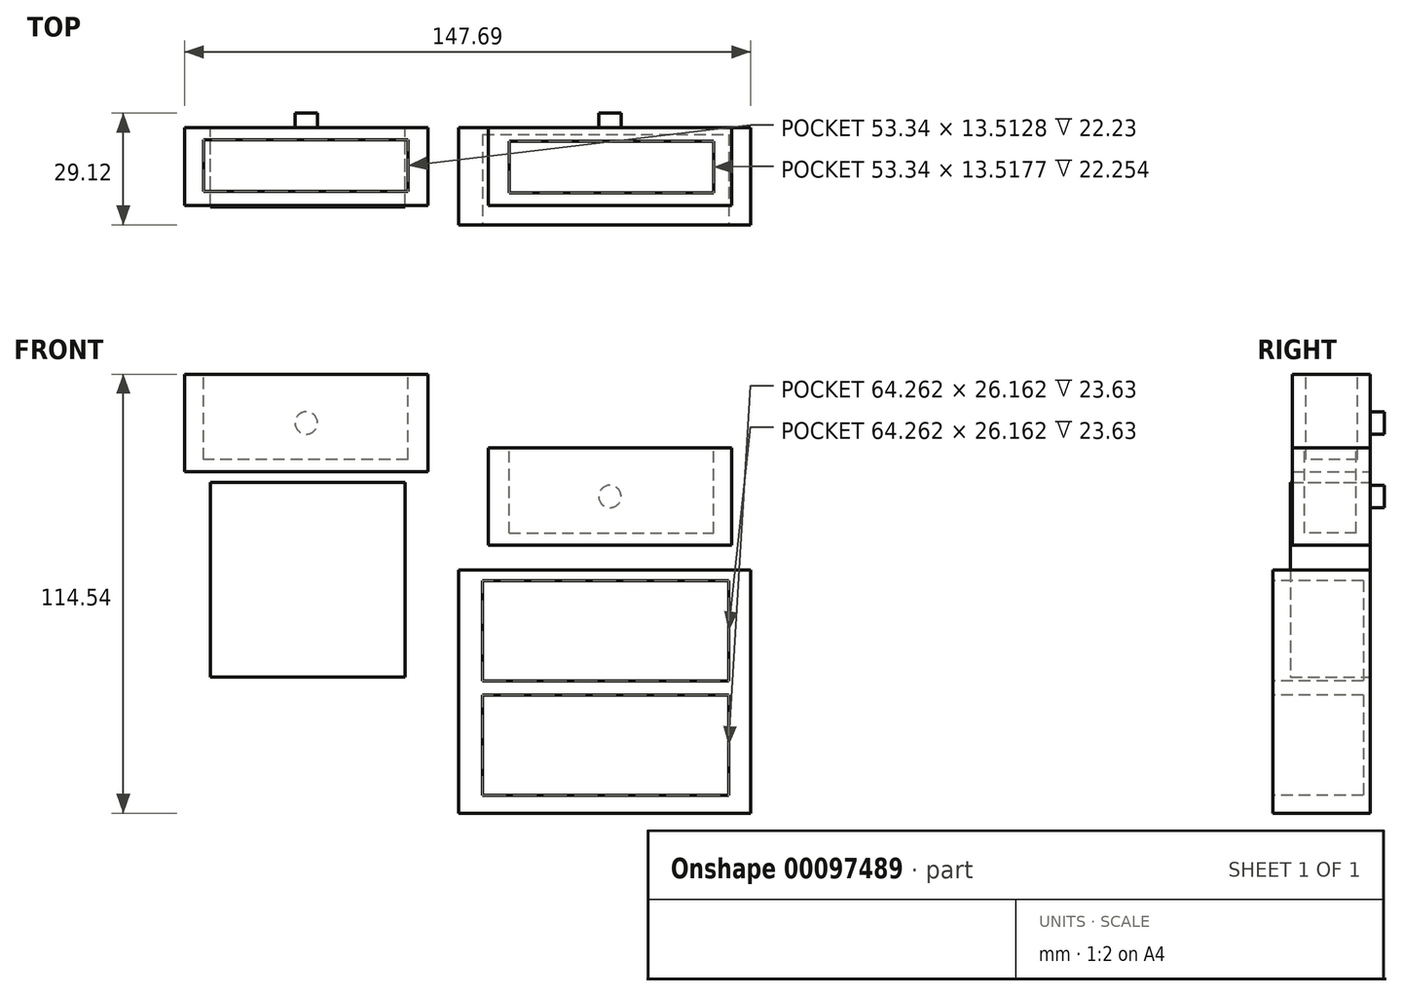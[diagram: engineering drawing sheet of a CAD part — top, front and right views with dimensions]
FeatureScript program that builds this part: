
annotation { "Feature Type Name" : "Feature", "Feature Type Description" : "" }
export const myFeature = defineFeature(function(context is Context, id is Id, definition is map)
    precondition{}
    {
        {
            var Q0;
            Q0=qCreatedBy(makeId("Front.planeOp"),FACE);
            var sketch = newSketch(context, id + "F0", { "sketchPlane" : qUnion([Q0])});
            skLineSegment(sketch, "E0.bottom", {"start": v(-64.78, 16.94) * mm, "end": v(-13.98, 16.94) * mm});
            skLineSegment(sketch, "E0.top", {"start": v(-64.78, -33.86) * mm, "end": v(-13.98, -33.86) * mm});
            skLineSegment(sketch, "E0.left", {"start": v(-64.78, 16.94) * mm, "end": v(-64.78, -33.86) * mm});
            skLineSegment(sketch, "E0.right", {"start": v(-13.98, 16.94) * mm, "end": v(-13.98, -33.86) * mm});
            skSolve(sketch);
        }
        {
            var Q0;
            Q0=makeQuery(id+"F0.imprint","IMPRINT",FACE,{"disambiguationData":[TD([[makeQuery(id+"F0.imprint","IMPRINT",EDGE,{"derivedFrom":sQuery(id+"F0.wireOp",EDGE,"E0.bottom")}),-1.0]])]});
            extrude(context, id + "F1", {"entities" : qUnion([Q0]), "depth" : 20.8 * mm});
        }
        {
            var Q0;
            Q0=qCreatedBy(makeId("Front.planeOp"),FACE);
            var sketch = newSketch(context, id + "F2", { "sketchPlane" : qUnion([Q0])});
            skLineSegment(sketch, "E1.bottom", {"start": v(-0.02, -5.87) * mm, "end": v(76.18, -5.87) * mm});
            skLineSegment(sketch, "E1.top", {"start": v(-0.02, -69.37) * mm, "end": v(76.18, -69.37) * mm});
            skLineSegment(sketch, "E1.left", {"start": v(-0.02, -5.87) * mm, "end": v(-0.02, -69.37) * mm});
            skLineSegment(sketch, "E1.right", {"start": v(76.18, -5.87) * mm, "end": v(76.18, -69.37) * mm});
            skSolve(sketch);
        }
        {
            var Q0;
            Q0 = qSketchRegion(id + "F2", true);
            extrude(context, id + "F3", {"entities" : qUnion([Q0]), "depth" : 25.4 * mm});
        }
        {
            var Q0;
            Q0=makeQuery(id+"F3.opExtrude","CAP_FACE",FACE,{"disambiguationData":[OSD([sQuery(id+"F2.wireOp",EDGE,"E1.bottom"),sQuery(id+"F2.wireOp",EDGE,"E1.top"),sQuery(id+"F2.wireOp",EDGE,"E1.left"),sQuery(id+"F2.wireOp",EDGE,"E1.right")])],"isStart":false});
            var sketch = newSketch(context, id + "F4", { "sketchPlane" : qUnion([Q0])});
            skLineSegment(sketch, "E2.bottom", {"start": v(6.26, -8.68) * mm, "end": v(70.52, -8.68) * mm});
            skLineSegment(sketch, "E2.top", {"start": v(6.26, -34.84) * mm, "end": v(70.52, -34.84) * mm});
            skLineSegment(sketch, "E2.left", {"start": v(6.26, -8.68) * mm, "end": v(6.26, -34.84) * mm});
            skLineSegment(sketch, "E2.right", {"start": v(70.52, -8.68) * mm, "end": v(70.52, -34.84) * mm});
            skLineSegment(sketch, "E3.bottom", {"start": v(6.26, -38.56) * mm, "end": v(70.52, -38.56) * mm});
            skLineSegment(sketch, "E3.top", {"start": v(6.26, -64.72) * mm, "end": v(70.52, -64.72) * mm});
            skLineSegment(sketch, "E3.left", {"start": v(6.26, -38.56) * mm, "end": v(6.26, -64.72) * mm});
            skLineSegment(sketch, "E3.right", {"start": v(70.52, -38.56) * mm, "end": v(70.52, -64.72) * mm});
            skSolve(sketch);
        }
        {
            var Q0;
            Q0=makeQuery(id+"F4.imprint","IMPRINT",FACE,{"disambiguationData":[TD([[makeQuery(id+"F4.imprint","IMPRINT",EDGE,{"derivedFrom":sQuery(id+"F4.wireOp",EDGE,"E2.bottom")}),-1.0]])]});
            var Q1;
            Q1=makeQuery(id+"F4.imprint","IMPRINT",FACE,{"disambiguationData":[TD([[makeQuery(id+"F4.imprint","IMPRINT",EDGE,{"derivedFrom":sQuery(id+"F4.wireOp",EDGE,"E3.bottom")}),-1.0]])]});
            extrude(context, id + "F5", {"entities" : qUnion([Q0, Q1]), "operationType" : NewBodyOperationType.REMOVE, "oppositeDirection" : true, "depth" : 23.63 * mm});
        }
        {
            var Q0;
            Q0=qCreatedBy(makeId("Front.planeOp"),FACE);
            var sketch = newSketch(context, id + "F6", { "sketchPlane" : qUnion([Q0])});
            skLineSegment(sketch, "E4.bottom", {"start": v(7.71, 25.97) * mm, "end": v(71.21, 25.97) * mm});
            skLineSegment(sketch, "E4.top", {"start": v(7.71, 0.57) * mm, "end": v(71.21, 0.57) * mm});
            skLineSegment(sketch, "E4.left", {"start": v(7.71, 25.97) * mm, "end": v(7.71, 0.57) * mm});
            skLineSegment(sketch, "E4.right", {"start": v(71.21, 25.97) * mm, "end": v(71.21, 0.57) * mm});
            skLineSegment(sketch, "E5.bottom", {"start": v(-88.9, 51.2) * mm, "end": v(-25.4, 51.2) * mm});
            skLineSegment(sketch, "E5.top", {"start": v(-88.9, 23.78) * mm, "end": v(-25.4, 23.78) * mm});
            skLineSegment(sketch, "E5.left", {"start": v(-88.9, 51.2) * mm, "end": v(-88.9, 23.78) * mm});
            skLineSegment(sketch, "E5.right", {"start": v(-25.4, 51.2) * mm, "end": v(-25.4, 23.78) * mm});
            skSolve(sketch);
        }
        {
            var Q0;
            Q0=makeQuery(id+"F6.imprint","IMPRINT",FACE,{"disambiguationData":[TD([[makeQuery(id+"F6.imprint","IMPRINT",EDGE,{"derivedFrom":sQuery(id+"F6.wireOp",EDGE,"E4.bottom")}),-1.0]])]});
            extrude(context, id + "F7", {"entities" : qUnion([Q0]), "depth" : 20.32 * mm});
        }
        {
            var Q0;
            Q0=qCreatedBy(makeId("Front.planeOp"),FACE);
            var sketch = newSketch(context, id + "F8", { "sketchPlane" : qUnion([Q0])});
            skLineSegment(sketch, "E6.bottom", {"start": v(-71.5, 45.17) * mm, "end": v(-8, 45.17) * mm});
            skLineSegment(sketch, "E6.top", {"start": v(-71.5, 19.77) * mm, "end": v(-8, 19.77) * mm});
            skLineSegment(sketch, "E6.left", {"start": v(-71.5, 45.17) * mm, "end": v(-71.5, 19.77) * mm});
            skLineSegment(sketch, "E6.right", {"start": v(-8, 45.17) * mm, "end": v(-8, 19.77) * mm});
            skSolve(sketch);
        }
        {
            var Q0;
            Q0 = qSketchRegion(id + "F8", true);
            extrude(context, id + "F9", {"entities" : qUnion([Q0]), "depth" : 20.32 * mm});
        }
        {
            var Q0;
            Q0=qCreatedBy(makeId("Front.planeOp"),FACE);
            var sketch = newSketch(context, id + "F10", { "sketchPlane" : qUnion([Q0])});
            skCircle(sketch, "E7", {"center": v(39.46, 13.27) * mm, "radius": 2.92 * mm});
            skCircle(sketch, "E8", {"center": v(-39.76, 32.47) * mm, "radius": 2.92 * mm});
            skSolve(sketch);
        }
        {
            var Q0;
            Q0=makeQuery(id+"F10.imprint","IMPRINT",FACE,{"disambiguationData":[TD([[makeQuery(id+"F10.imprint","IMPRINT",EDGE,{"derivedFrom":sQuery(id+"F10.wireOp",EDGE,"E7")}),1.0]])]});
            var Q1;
            Q1=makeQuery(id+"F10.imprint","IMPRINT",FACE,{"disambiguationData":[TD([[makeQuery(id+"F10.imprint","IMPRINT",EDGE,{"derivedFrom":sQuery(id+"F10.wireOp",EDGE,"E8")}),1.0]])]});
            extrude(context, id + "F11", {"entities" : qUnion([Q0, Q1]), "oppositeDirection" : true, "depth" : 3.72 * mm});
        }
        {
            var Q0;
            Q0=makeQuery(id+"F7.opExtrude","SWEPT_FACE",FACE,{"disambiguationData":[OSD([sQuery(id+"F6.wireOp",EDGE,"E4.bottom")])]});
            var sketch = newSketch(context, id + "F12", { "sketchPlane" : qUnion([Q0])});
            skLineSegment(sketch, "E9.bottom", {"start": v(13.19, -3.6) * mm, "end": v(66.53, -3.6) * mm});
            skLineSegment(sketch, "E9.top", {"start": v(13.19, -17.12) * mm, "end": v(66.53, -17.12) * mm});
            skLineSegment(sketch, "E9.left", {"start": v(13.19, -3.6) * mm, "end": v(13.19, -17.12) * mm});
            skLineSegment(sketch, "E9.right", {"start": v(66.53, -3.6) * mm, "end": v(66.53, -17.12) * mm});
            skSolve(sketch);
        }
        {
            var Q0;
            Q0=makeQuery(id+"F12.imprint","IMPRINT",FACE,{"disambiguationData":[TD([[makeQuery(id+"F12.imprint","IMPRINT",EDGE,{"derivedFrom":sQuery(id+"F12.wireOp",EDGE,"E9.bottom")}),-1.0]])]});
            extrude(context, id + "F13", {"entities" : qUnion([Q0]), "operationType" : NewBodyOperationType.REMOVE, "oppositeDirection" : true, "depth" : 22.25 * mm});
        }
        {
            var Q0;
            Q0=makeQuery(id+"F9.opExtrude","SWEPT_FACE",FACE,{"disambiguationData":[OSD([sQuery(id+"F8.wireOp",EDGE,"E6.bottom")])]});
            var sketch = newSketch(context, id + "F14", { "sketchPlane" : qUnion([Q0])});
            skLineSegment(sketch, "E10.bottom", {"start": v(-13.22, -3.2) * mm, "end": v(-66.56, -3.2) * mm});
            skLineSegment(sketch, "E10.top", {"start": v(-13.22, -16.72) * mm, "end": v(-66.56, -16.72) * mm});
            skLineSegment(sketch, "E10.left", {"start": v(-13.22, -3.2) * mm, "end": v(-13.22, -16.72) * mm});
            skLineSegment(sketch, "E10.right", {"start": v(-66.56, -3.2) * mm, "end": v(-66.56, -16.72) * mm});
            skSolve(sketch);
        }
        {
            var Q0;
            Q0=makeQuery(id+"F14.imprint","IMPRINT",FACE,{"disambiguationData":[TD([[makeQuery(id+"F14.imprint","IMPRINT",EDGE,{"derivedFrom":sQuery(id+"F14.wireOp",EDGE,"E10.bottom")}),1.0]])]});
            extrude(context, id + "F15", {"entities" : qUnion([Q0]), "operationType" : NewBodyOperationType.REMOVE, "oppositeDirection" : true, "depth" : 22.23 * mm});
        }
    });
